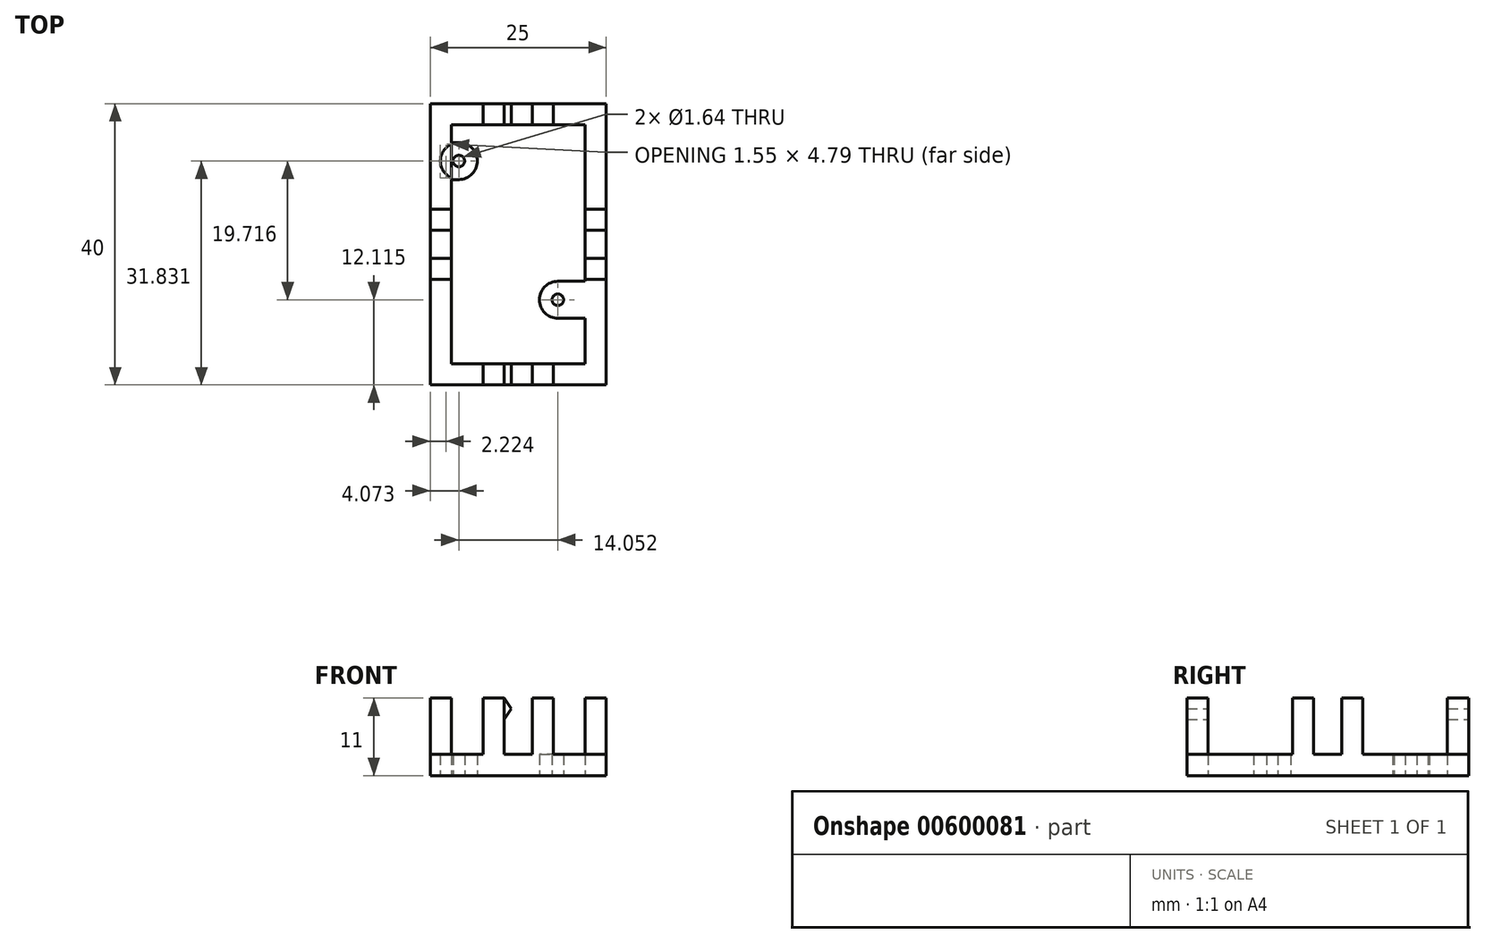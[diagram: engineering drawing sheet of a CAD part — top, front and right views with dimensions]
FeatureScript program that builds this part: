
annotation { "Feature Type Name" : "Feature", "Feature Type Description" : "" }
export const myFeature = defineFeature(function(context is Context, id is Id, definition is map)
    precondition{}
    {
        {
            var Q0;
            Q0=qCreatedBy(makeId("Top.planeOp"),FACE);
            var sketch = newSketch(context, id + "F0", { "sketchPlane" : qUnion([Q0])});
            skLineSegment(sketch, "E0.bottom", {"start": v(-9.5, 17) * mm, "end": v(9.5, 17) * mm});
            skLineSegment(sketch, "E0.top", {"start": v(-9.5, -17) * mm, "end": v(9.5, -17) * mm});
            skLineSegment(sketch, "E0.left", {"start": v(-9.5, 17) * mm, "end": v(-9.5, -17) * mm});
            skLineSegment(sketch, "E0.right", {"start": v(9.5, 17) * mm, "end": v(9.5, -17) * mm});
            skLineSegment(sketch, "E1.bottom", {"start": v(-12.5, 20) * mm, "end": v(12.5, 20) * mm});
            skLineSegment(sketch, "E1.top", {"start": v(-12.5, -20) * mm, "end": v(12.5, -20) * mm});
            skLineSegment(sketch, "E1.left", {"start": v(-12.5, 20) * mm, "end": v(-12.5, -20) * mm});
            skLineSegment(sketch, "E1.right", {"start": v(12.5, 20) * mm, "end": v(12.5, -20) * mm});
            skCircle(sketch, "E2", {"center": v(-8.43, 11.83) * mm, "radius": 2.62 * mm});
            skCircle(sketch, "E3", {"center": v(-8.43, 11.83) * mm, "radius": 0.82 * mm});
            skLineSegment(sketch, "E4", {"start": v(-8.43, 14.46) * mm, "end": v(-9.5, 14.46) * mm});
            skLineSegment(sketch, "E5", {"start": v(-8.43, 9.2) * mm, "end": v(-9.5, 9.2) * mm});
            skCircle(sketch, "E6", {"center": v(5.62, -7.89) * mm, "radius": 2.62 * mm});
            skCircle(sketch, "E7", {"center": v(5.62, -7.89) * mm, "radius": 0.82 * mm});
            skLineSegment(sketch, "E8", {"start": v(5.62, -5.26) * mm, "end": v(9.5, -5.26) * mm});
            skLineSegment(sketch, "E9", {"start": v(5.62, -10.5) * mm, "end": v(9.5, -10.5) * mm});
            skSolve(sketch);
        }
        {
            var Q0;
            {var subQ3=sQuery(id+"F0.wireOp",EDGE,"E4");Q0=makeQuery(id+"F0.imprint","IMPRINT",FACE,{"disambiguationData":[TD([[makeQuery(id+"F0.imprint","IMPRINT",EDGE,{"derivedFrom":subQ3}),1.0]])]});}
            var Q1;
            Q1=makeQuery(id+"F0.imprint","IMPRINT",FACE,{"disambiguationData":[TD([[makeQuery(id+"F0.imprint","IMPRINT",EDGE,{"derivedFrom":sQuery(id+"F0.wireOp",EDGE,"E3")}),-1.0]])]});
            var Q2;
            {var subQ0=sQuery(id+"F0.wireOp",EDGE,"E2");var subQ1=sQuery(id+"F0.wireOp",EDGE,"E0.left");var subQ3=makeQuery(id+"F0.imprint","INTERSECT",VERTEX,{"disambiguationData":[OD(0.0)],"derivedFrom":[subQ1,subQ0]});Q2=makeQuery(id+"F0.imprint","IMPRINT",FACE,{"disambiguationData":[TD([[makeQuery(id+"F0.imprint","IMPRINT",EDGE,{"disambiguationData":[TD([[subQ3,-1.0]])],"derivedFrom":subQ1}),-1.0]])]});}
            var Q3;
            {var subQ10=sQuery(id+"F0.wireOp",EDGE,"E0.bottom");Q3=makeQuery(id+"F0.imprint","IMPRINT",FACE,{"disambiguationData":[TD([[makeQuery(id+"F0.imprint","IMPRINT",EDGE,{"derivedFrom":subQ10}),1.0]])]});}
            var Q4;
            {var subQ0=sQuery(id+"F0.wireOp",EDGE,"E5");Q4=makeQuery(id+"F0.imprint","IMPRINT",FACE,{"disambiguationData":[TD([[makeQuery(id+"F0.imprint","IMPRINT",EDGE,{"derivedFrom":subQ0}),-1.0]])]});}
            var Q5;
            {var subQ1=sQuery(id+"F0.wireOp",EDGE,"E8");Q5=makeQuery(id+"F0.imprint","IMPRINT",FACE,{"disambiguationData":[TD([[makeQuery(id+"F0.imprint","IMPRINT",EDGE,{"derivedFrom":subQ1}),-1.0]])]});}
            var Q6;
            Q6=makeQuery(id+"F0.imprint","IMPRINT",FACE,{"disambiguationData":[TD([[makeQuery(id+"F0.imprint","IMPRINT",EDGE,{"derivedFrom":sQuery(id+"F0.wireOp",EDGE,"E7")}),-1.0]])]});
            extrude(context, id + "F1", {"entities" : qUnion([Q0, Q1, Q2, Q3, Q4, Q5, Q6]), "depth" : 3 * mm});
        }
        {
            var Q0;
            Q0=qCreatedBy(makeId("Top.planeOp"),FACE);
            var sketch = newSketch(context, id + "F2", { "sketchPlane" : qUnion([Q0])});
            skLineSegment(sketch, "E10.bottom", {"start": v(-12.5, 5) * mm, "end": v(-9.5, 5) * mm});
            skLineSegment(sketch, "E10.top", {"start": v(-12.5, 2) * mm, "end": v(-9.5, 2) * mm});
            skLineSegment(sketch, "E10.left", {"start": v(-12.5, 5) * mm, "end": v(-12.5, 2) * mm});
            skLineSegment(sketch, "E10.right", {"start": v(-9.5, 5) * mm, "end": v(-9.5, 2) * mm});
            skLineSegment(sketch, "E11.bottom", {"start": v(9.5, 5) * mm, "end": v(12.5, 5) * mm});
            skLineSegment(sketch, "E11.top", {"start": v(9.5, 2) * mm, "end": v(12.5, 2) * mm});
            skLineSegment(sketch, "E11.left", {"start": v(9.5, 5) * mm, "end": v(9.5, 2) * mm});
            skLineSegment(sketch, "E11.right", {"start": v(12.5, 5) * mm, "end": v(12.5, 2) * mm});
            skLineSegment(sketch, "E12.bottom", {"start": v(-12.5, -2) * mm, "end": v(-9.5, -2) * mm});
            skLineSegment(sketch, "E12.top", {"start": v(-12.5, -5) * mm, "end": v(-9.5, -5) * mm});
            skLineSegment(sketch, "E12.left", {"start": v(-12.5, -2) * mm, "end": v(-12.5, -5) * mm});
            skLineSegment(sketch, "E12.right", {"start": v(-9.5, -2) * mm, "end": v(-9.5, -5) * mm});
            skLineSegment(sketch, "E13.bottom", {"start": v(9.5, -2) * mm, "end": v(12.5, -2) * mm});
            skLineSegment(sketch, "E13.top", {"start": v(9.5, -5) * mm, "end": v(12.5, -5) * mm});
            skLineSegment(sketch, "E13.left", {"start": v(9.5, -2) * mm, "end": v(9.5, -5) * mm});
            skLineSegment(sketch, "E13.right", {"start": v(12.5, -2) * mm, "end": v(12.5, -5) * mm});
            skLineSegment(sketch, "E14.bottom", {"start": v(-5, 20) * mm, "end": v(-2, 20) * mm});
            skLineSegment(sketch, "E14.top", {"start": v(-5, 17) * mm, "end": v(-2, 17) * mm});
            skLineSegment(sketch, "E14.left", {"start": v(-5, 20) * mm, "end": v(-5, 17) * mm});
            skLineSegment(sketch, "E14.right", {"start": v(-2, 20) * mm, "end": v(-2, 17) * mm});
            skLineSegment(sketch, "E15.top", {"start": v(2, 17) * mm, "end": v(5, 17) * mm});
            skLineSegment(sketch, "E15.left", {"start": v(2, 20) * mm, "end": v(2, 17) * mm});
            skLineSegment(sketch, "E15.bottom", {"start": v(2, 20) * mm, "end": v(5, 20) * mm});
            skLineSegment(sketch, "E15.right", {"start": v(5, 20) * mm, "end": v(5, 17) * mm});
            skLineSegment(sketch, "E16.bottom", {"start": v(-5, -17) * mm, "end": v(-2, -17) * mm});
            skLineSegment(sketch, "E17.right", {"start": v(5, -17) * mm, "end": v(5, -20) * mm});
            skLineSegment(sketch, "E16.top", {"start": v(-5, -20) * mm, "end": v(-2, -20) * mm});
            skLineSegment(sketch, "E17.bottom", {"start": v(2, -17) * mm, "end": v(5, -17) * mm});
            skLineSegment(sketch, "E17.left", {"start": v(2, -17) * mm, "end": v(2, -20) * mm});
            skLineSegment(sketch, "E17.top", {"start": v(2, -20) * mm, "end": v(5, -20) * mm});
            skLineSegment(sketch, "E16.right", {"start": v(-2, -17) * mm, "end": v(-2, -20) * mm});
            skLineSegment(sketch, "E16.left", {"start": v(-5, -17) * mm, "end": v(-5, -20) * mm});
            skSolve(sketch);
        }
        {
            var Q0;
            Q0=qSketchRegion(id+"F2",true);
            extrude(context, id + "F3", {"entities" : qUnion([Q0]), "operationType" : NewBodyOperationType.ADD, "depth" : 11 * mm});
        }
        {
            var Q0;
            Q0=makeQuery(id+"F3.boolean.opBoolean","MERGE",FACE,{"derivedFrom":[makeQuery(id+"F1.opExtrude","SWEPT_FACE",FACE,{"disambiguationData":[OSD([sQuery(id+"F0.wireOp",EDGE,"E1.bottom")])]}),makeQuery(id+"F3.opExtrude","SWEPT_FACE",FACE,{"disambiguationData":[OSD([sQuery(id+"F2.wireOp",EDGE,"E14.bottom")])]}),makeQuery(id+"F3.opExtrude","SWEPT_FACE",FACE,{"disambiguationData":[OSD([sQuery(id+"F2.wireOp",EDGE,"E15.bottom")])]})]});
            var sketch = newSketch(context, id + "F4", { "sketchPlane" : qUnion([Q0])});
            skLineSegment(sketch, "E18", {"start": v(2, 11) * mm, "end": v(1, 9.5) * mm});
            skLineSegment(sketch, "E19", {"start": v(1, 9.5) * mm, "end": v(2, 8) * mm});
            skSolve(sketch);
        }
        {
            var Q0;
            {var subQ3=sQuery(id+"F4.wireOp",EDGE,"E18");Q0=makeQuery(id+"F4.imprint","IMPRINT",FACE,{"disambiguationData":[TD([[makeQuery(id+"F4.imprint","IMPRINT",EDGE,{"derivedFrom":subQ3}),1.0]])]});}
            extrude(context, id + "F5", {"entities" : qUnion([Q0]), "oppositeDirection" : true, "depth" : 3 * mm});
        }
        {
            var Q0;
            Q0=makeQuery(id+"F3.boolean.opBoolean","MERGE",FACE,{"derivedFrom":[makeQuery(id+"F1.opExtrude","SWEPT_FACE",FACE,{"disambiguationData":[OSD([sQuery(id+"F0.wireOp",EDGE,"E0.top")])]}),makeQuery(id+"F3.opExtrude","SWEPT_FACE",FACE,{"disambiguationData":[OSD([sQuery(id+"F2.wireOp",EDGE,"E16.bottom")])]}),makeQuery(id+"F3.opExtrude","SWEPT_FACE",FACE,{"disambiguationData":[OSD([sQuery(id+"F2.wireOp",EDGE,"E17.bottom")])]})]});
            var sketch = newSketch(context, id + "F6", { "sketchPlane" : qUnion([Q0])});
            skLineSegment(sketch, "E20", {"start": v(2, 11) * mm, "end": v(1, 9.5) * mm});
            skLineSegment(sketch, "E21", {"start": v(1, 9.5) * mm, "end": v(2, 8) * mm});
            skSolve(sketch);
        }
        {
            var Q0;
            {var subQ3=sQuery(id+"F6.wireOp",EDGE,"E20");Q0=makeQuery(id+"F6.imprint","IMPRINT",FACE,{"disambiguationData":[TD([[makeQuery(id+"F6.imprint","IMPRINT",EDGE,{"derivedFrom":subQ3}),1.0]])]});}
            extrude(context, id + "F7", {"entities" : qUnion([Q0]), "oppositeDirection" : true, "depth" : 3 * mm});
        }
    });
